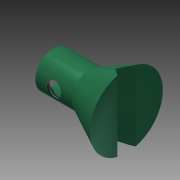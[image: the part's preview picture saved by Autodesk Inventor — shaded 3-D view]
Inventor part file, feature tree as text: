
AUTODESK INVENTOR PART (.ipt)
format: ipt  version: 2015 (Build 190159000, 159)  size: 124,416 bytes
history: native  units: mm
features: sketch x5, extrude x4, projected_geometry x3, loft x1, thread x1
ambient origin geometry x8: Origin, YZ Plane, XZ Plane, XY Plane, X Axis, Y Axis, Z Axis, Center Point
bodies: Solid1 (feature_tree)
feature tree (14):
  extrude  "Extrusion1"  Depth=10.0mm
  sketch  "Sketch2"  dims[d2=10.0mm d3=0.0mm d4=10.0mm d5=0.0mm]
  extrude  "Extrusion2"  Depth=10.0mm TaperAngle=0.0deg
  loft  "Loft1"
  extrude  "Extrusion3"  Depth=5.0mm
  extrude  "Extrusion4"  Depth=20.0mm TaperAngle=0.0deg
  thread  "Thread1"  [1 undecoded]
  sketch  "Sketch1"  dims[d0=8.0mm d1=10.0mm]
  projected_geometry  "Projected Loop1"
  sketch  "Sketch3"  dims[d6=20.0mm d7=0.0mm d8=90.0deg]
  sketch  "Sketch4"  dims[d9=0.0mm d10=90.0deg d11=5.0mm]
  projected_geometry  "Projected Loop2"
  sketch  "Sketch5"  dims[d12=3.0mm d13=20.0mm d14=0.0mm d15=4.0mm d16=5.0mm d17=20.0mm d18=0.0mm d19=10.0mm d20=0.0mm]
  projected_geometry  "Projected Loop3"
note: 1 required parameter value undecoded (feature->parameter linkage not recoverable at this tier; creation-order binding heuristic only, values carry confidence <= 0.55)
